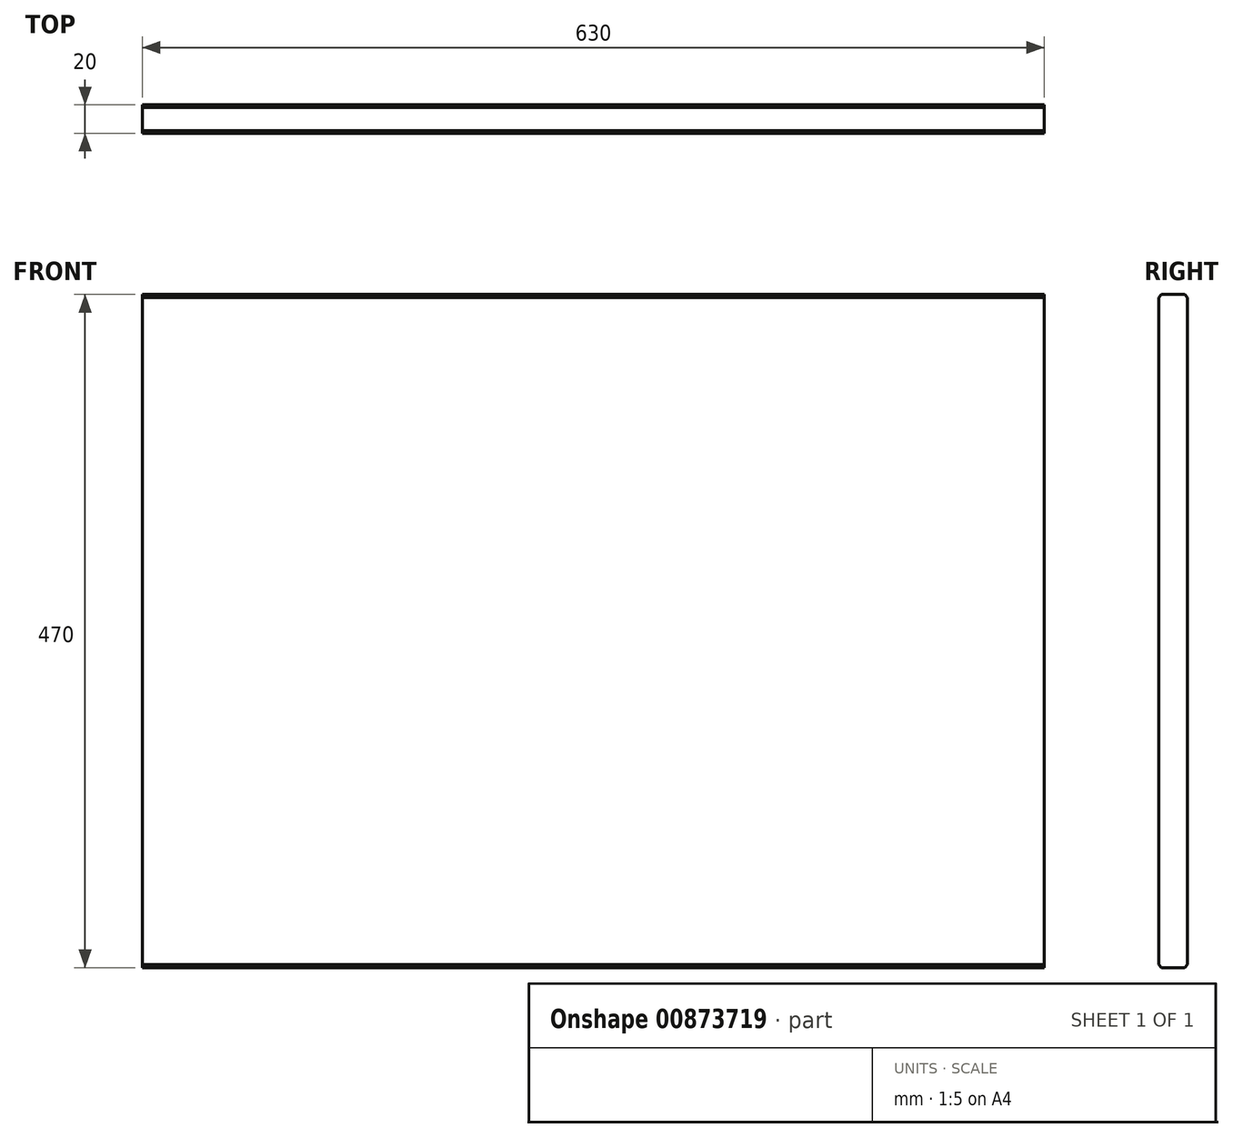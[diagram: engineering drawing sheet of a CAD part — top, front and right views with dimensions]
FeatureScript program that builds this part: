
annotation { "Feature Type Name" : "Feature", "Feature Type Description" : "" }
export const myFeature = defineFeature(function(context is Context, id is Id, definition is map)
    precondition{}
    {
        {
            var Q0;
            Q0=qCreatedBy(makeId("Front.planeOp"),FACE);
            var sketch = newSketch(context, id + "F0", { "sketchPlane" : qUnion([Q0])});
            skLineSegment(sketch, "E0.bottom", {"start": v(0, 0) * mm, "end": v(630, 0) * mm});
            skLineSegment(sketch, "E0.top", {"start": v(0, 470) * mm, "end": v(630, 470) * mm});
            skLineSegment(sketch, "E0.left", {"start": v(0, 0) * mm, "end": v(0, 470) * mm});
            skLineSegment(sketch, "E0.right", {"start": v(630, 0) * mm, "end": v(630, 470) * mm});
            skSolve(sketch);
        }
        {
            var Q0;
            Q0 = qSketchRegion(id + "F0", true);
            extrude(context, id + "F1", {"entities" : qUnion([Q0]), "depth" : 20 * mm, "offsetDistance" : 25 * mm});
        }
        {
            var Q0;
            Q0=makeQuery(id+"F1.opExtrude","CAP_EDGE",EDGE,{"disambiguationData":[OSD([sQuery(id+"F0.wireOp",EDGE,"E0.top")])],"isStart":true});
            var Q1;
            Q1=makeQuery(id+"F1.opExtrude","CAP_EDGE",EDGE,{"disambiguationData":[OSD([sQuery(id+"F0.wireOp",EDGE,"E0.top")])],"isStart":false});
            var Q2;
            Q2=makeQuery(id+"F1.opExtrude","CAP_EDGE",EDGE,{"disambiguationData":[OSD([sQuery(id+"F0.wireOp",EDGE,"E0.bottom")])],"isStart":true});
            var Q3;
            Q3=makeQuery(id+"F1.opExtrude","CAP_EDGE",EDGE,{"disambiguationData":[OSD([sQuery(id+"F0.wireOp",EDGE,"E0.bottom")])],"isStart":false});
            chamfer(context, id + "F2", {"entities" : qUnion([Q0, Q1, Q2, Q3]), "width" : 2 * mm, "tangentPropagation" : true});
        }
    });
